# Revit family: IS_Conca_T3933_BIM_IT
name_source: partatom
category: Plumbing Fixtures
revit_build: Autodesk Revit 2017 (Build: 20160225_1515(x64)
units: mm (PartAtom-declared; Revit-internal decimal feet)

## family parameters
Always vertical = No
Cut with Voids When Loaded = No
OmniClass Number = 23.45.05.14.21.11
OmniClass Title = Bath/Shower Units
Part Type = Normal
Room Calculation Point = No
Round Connector Dimension = Use Diameter
Shared = No
Work Plane-Based = No

## types (6) — shared parameters
Accessori = https://www.idealstandard.it
Aiuto = https://www.idealstandard.it
AltezzaNominale = 370 mm
Autore = Ideal Standard
BIMobject category = Storage
BIMobject category code = sanitary-storage
BIMobject main category = Sanitary
BIMobject main category code = sanitary
Brand = https://www.idealstandard.it
Caratteristiche = Mobile sottolavabo, 1200 x 505 x 370mm, 1 cassetto esterno senza piano da appoggio
Description = Vanity unit, 1200 x 505 x 370mm, 1 external drawer without countertop
DescrizioneClassifcazioneUni2015 = Bathroom cabinets
Desrizione = Mobile sottolavabo, 1200 x 505 x 370mm, 1 cassetto esterno senza piano da appoggio
DurataGaranzia = 2
DurataGaranziaProdotti = 2
Forma = Rettangolare
Garanzia = Garanzia Idealstandard
IfcEsportaCome = IfcFurnitureType
InformaziniGaranzia = https://www.idealstandard.it
InformazioniDiProdotto = http://www.idealstandard.it
InformazioniGaranzia = https://www.idealstandard.it
Installation instructions = https://www.idealspec.co.uk
InstruzioniInstallazione = https://www.idealstandard.it
LarghezzaNominale = 1202 mm
Maniglia = No
Manufacturer = Ideal Standard
Materiale = Ceramics
NominalDepth = 505 mm  [stored 1.65682 ft]
NominalHeight = 359 mm
NominalWidth = 1200 mm
PesoNetto = 36.5
PiattoDoccia = No
Product group = Bathroom_Furniture
Produttore = Ideal Standard
ProfonditaNominale = 505 mm  [stored 1.65682 ft]
Revisione = 1
RiferimentoClassificazioneUni2015 = Pr_40_30_78_03
Spazio = Interno
Telefono = 800 652 290
TipoEspotazioneIfc = Bathroom cabinets
URL = https://www.ideal-standard.co.uk
Uniclass 2015 Code = Pr_40_30_78_03
Uniclass 2015 Name = Bathroom cabinets
UnitàDurata = Anno
UnitàDurataGaranzia = Anno
UnitàLineare = Milimitre
UnitàMonetaria = €
UnitàSuperficie = Milimitre
UnitàVolume = Litri
Versione = 1
VersioneClassificazioneUni2015 = v1.1
zero-valued in all types: CostoDiSostituzione, DimensioneScarico, LunghezzaNominale, Nominal depth, Nominal height, SeatMaterial, SpessoreDelMateriale, SpilloverLivello, Weight Net (Kg)

## per-type parameters (varying)
| type | CodiceABarre | CodiceArticolo | Colore | Finitura | Model | ModelloDiRiferimento | Nome | NomeOggettoBim | NumeroDiModello |
| T3933Y1 - Conca BSN UN 120X50X37 1 DR NOWTOP  WHMT - T3933 - Y1_MattWhite | 8014140460312 | T3933Y1 | Matt white | Matt white | T3933Y1 | T3933Y1 | BathroomCabinets_Conca_T3933Y1_IdealStandard | ISI_IdealStandard_Bathroom Cabinets_Conca_T3933Y1 | T3933Y1 |
| T3933Y2 - Conca BSN UN 120X50X37 1 DR NOWTOP  WHMT - T3933 - Y2_MattAntracite | 8014140460329 | T3933Y2 | Matt anthracite | Matt anthracite | T3933Y2 | T3933Y2 | BathroomCabinets_Conca_T3933Y2_IdealStandard | ISI_IdealStandard_Bathroom Cabinets_Conca_T3933Y2 | T3933Y2 |
| T3933Y3 - Conca BSN UN 120X50X37 1 DR NOWTOP  WHMT - T3933 - Y3_MattSunset | 8014140460336 | T3933Y3 | Matt Sunset | Matt Sunset | T3933Y3 | T3933Y3 | BathroomCabinets_Conca_T3933Y3_IdealStandard | ISI_IdealStandard_Bathroom Cabinets_Conca_T3933Y3 | T3933Y3 |
| T3933Y4 - Conca BSN UN 120X50X37 1 DR NOWTOP  WHMT - T3933 - Y4_SmokedOac | 8014140460343 | T3933Y4 | Smoked Oak | Smoked Oak | T3933Y4 | T3933Y4 | BathroomCabinets_Conca_T3933Y4_IdealStandard | ISI_IdealStandard_Bathroom Cabinets_Conca_T3933Y4 | T3933Y4 |
| T3933Y5 - Conca BSN UN 120X50X37 1 DR NOWTOP  WHMT - T3933 - Y5_DarkWalnut | 8014140460350 | T3933Y5 | Dark Walnut | Dark Walnut | T3933Y5 | T3933Y5 | BathroomCabinets_Conca_T3933Y5_IdealStandard | ISI_IdealStandard_Bathroom Cabinets_Conca_T3933Y5 | T3933Y5 |
| T3933Y6 - Conca BSN UN 120X50X37 1 DR NOWTOP  WHMT - T3933 - Y6_LightOak | 8014140460367 | T3933Y6 | Light Oak | Light Oak | T3933Y6 | T3933Y6 | BathroomCabinets_Conca_T3933Y6_IdealStandard | ISI_IdealStandard_Bathroom Cabinets_Conca_T3933Y6 | T3933Y6 |

note: [stored X ft] marks values corroborated as IEEE doubles in the binary element streams (Revit-internal decimal feet)

## geometry (parser evidence)
native form markers: Sweep x3
no freeform markers — native parametric forms only
